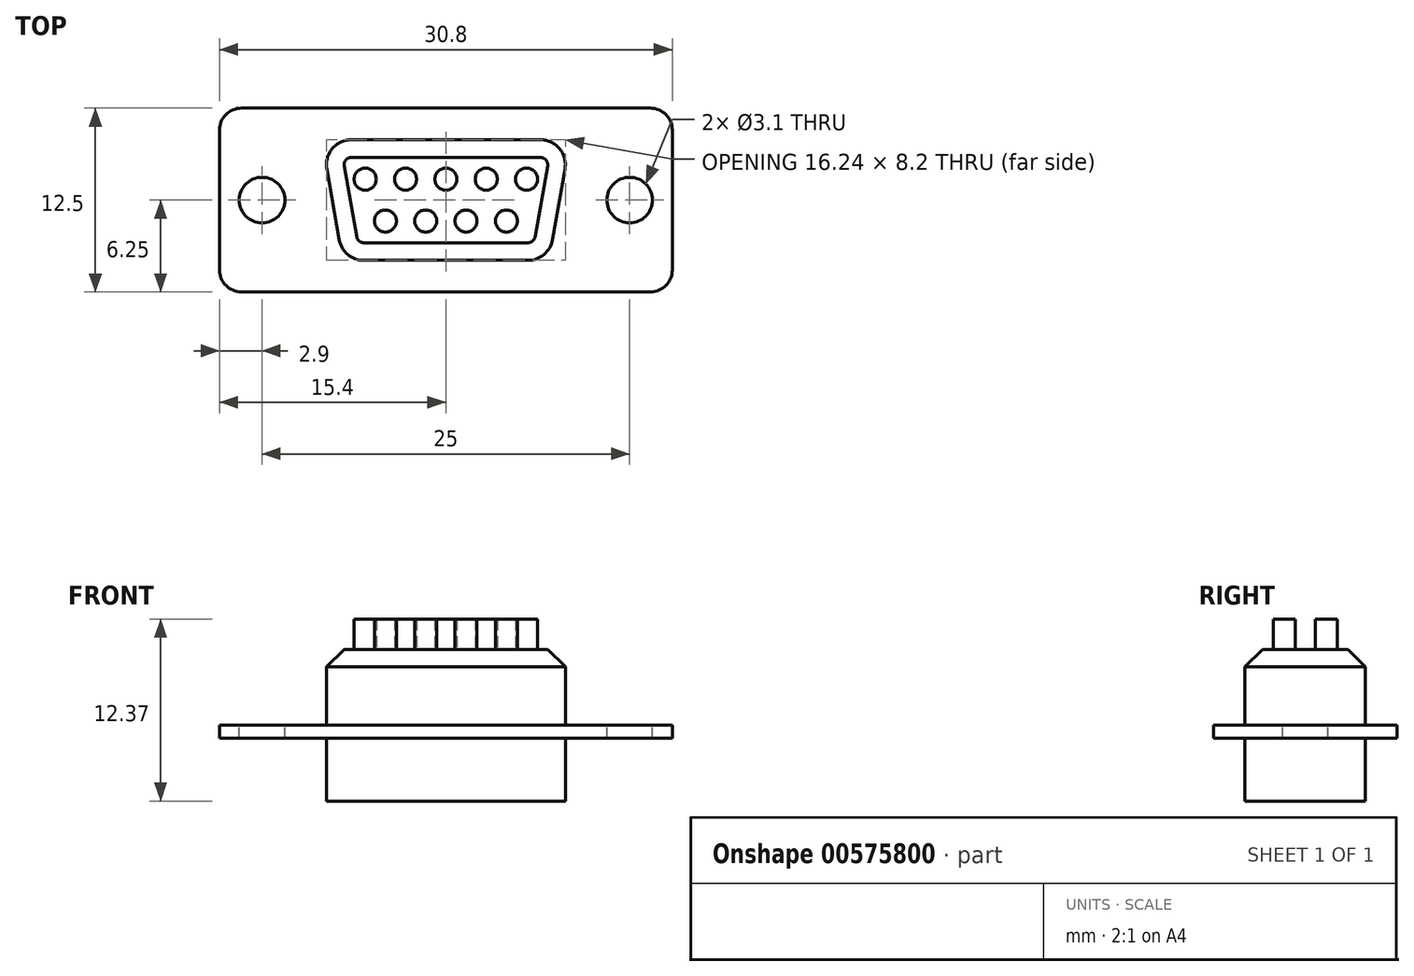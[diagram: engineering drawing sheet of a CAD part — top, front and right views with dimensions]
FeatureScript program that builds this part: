
annotation { "Feature Type Name" : "Feature", "Feature Type Description" : "" }
export const myFeature = defineFeature(function(context is Context, id is Id, definition is map)
    precondition{}
    {
        {
            var Q0;
            Q0=qCreatedBy(makeId("Top.planeOp"),FACE);
            var sketch = newSketch(context, id + "F0", { "sketchPlane" : qUnion([Q0])});
            skLineSegment(sketch, "E0.bottom", {"start": v(15.4, 6.25) * mm, "end": v(-15.4, 6.25) * mm});
            skLineSegment(sketch, "E0.top", {"start": v(15.4, -6.25) * mm, "end": v(-15.4, -6.25) * mm});
            skLineSegment(sketch, "E0.left", {"start": v(15.4, 6.25) * mm, "end": v(15.4, -6.25) * mm});
            skLineSegment(sketch, "E0.right", {"start": v(-15.4, 6.25) * mm, "end": v(-15.4, -6.25) * mm});
            skPoint(sketch, "E0.middle", {"position": v(0, 0) * mm});
            skSolve(sketch);
        }
        {
            var Q0;
            Q0=makeQuery(id+"F0.imprint","IMPRINT",FACE,{"disambiguationData":[TD([[makeQuery(id+"F0.imprint","IMPRINT",EDGE,{"derivedFrom":sQuery(id+"F0.wireOp",EDGE,"E0.bottom")}),1.0]])]});
            extrude(context, id + "F1", {"entities" : qUnion([Q0]), "depth" : 0.9 * mm, "offsetDistance" : 25.4 * mm});
        }
        {
            var Q0;
            Q0=makeQuery(id+"F1.opExtrude","SWEPT_EDGE",EDGE,{"disambiguationData":[OSD([sQuery(id+"F0.wireOp",EDGE,"E0.bottom"),sQuery(id+"F0.wireOp",EDGE,"E0.right")])]});
            var Q1;
            Q1=makeQuery(id+"F1.opExtrude","SWEPT_EDGE",EDGE,{"disambiguationData":[OSD([sQuery(id+"F0.wireOp",EDGE,"E0.bottom"),sQuery(id+"F0.wireOp",EDGE,"E0.left")])]});
            var Q2;
            Q2=makeQuery(id+"F1.opExtrude","SWEPT_EDGE",EDGE,{"disambiguationData":[OSD([sQuery(id+"F0.wireOp",EDGE,"E0.top"),sQuery(id+"F0.wireOp",EDGE,"E0.left")])]});
            var Q3;
            Q3=makeQuery(id+"F1.opExtrude","SWEPT_EDGE",EDGE,{"disambiguationData":[OSD([sQuery(id+"F0.wireOp",EDGE,"E0.top"),sQuery(id+"F0.wireOp",EDGE,"E0.right")])]});
            fillet(context, id + "F2", {"entities" : qUnion([Q0, Q1, Q2, Q3]), "radius" : 1.5 * mm, "tangentPropagation" : true, "allowEdgeOverflow" : false});
        }
        {
            var Q0;
            Q0=makeQuery(id+"F1.opExtrude","CAP_FACE",FACE,{"disambiguationData":[OSD([sQuery(id+"F0.wireOp",EDGE,"E0.bottom"),sQuery(id+"F0.wireOp",EDGE,"E0.top"),sQuery(id+"F0.wireOp",EDGE,"E0.left"),sQuery(id+"F0.wireOp",EDGE,"E0.right")])],"isStart":false});
            var sketch = newSketch(context, id + "F3", { "sketchPlane" : qUnion([Q0])});
            skLineSegment(sketch, "E1.bottom", {"start": v(8.45, 4.1) * mm, "end": v(-8.45, 4.1) * mm, "construction": true});
            skLineSegment(sketch, "E1.top", {"start": v(8.45, -4.1) * mm, "end": v(-8.45, -4.1) * mm, "construction": true});
            skLineSegment(sketch, "E1.left", {"start": v(8.45, 4.1) * mm, "end": v(8.45, -4.1) * mm, "construction": true});
            skLineSegment(sketch, "E1.right", {"start": v(-8.45, 4.1) * mm, "end": v(-8.45, -4.1) * mm, "construction": true});
            skPoint(sketch, "E1.middle", {"position": v(0, 0) * mm});
            skLineSegment(sketch, "E2", {"start": v(-8.45, 4.1) * mm, "end": v(8.45, 4.1) * mm});
            skLineSegment(sketch, "E3", {"start": v(-8.45, 4.1) * mm, "end": v(-7, -4.1) * mm});
            skLineSegment(sketch, "E4", {"start": v(8.45, 4.1) * mm, "end": v(7, -4.1) * mm});
            skLineSegment(sketch, "E5", {"start": v(-7, -4.1) * mm, "end": v(7, -4.1) * mm});
            skSolve(sketch);
        }
        {
            var Q0;
            Q0=makeQuery(id+"F3.imprint","IMPRINT",FACE,{"disambiguationData":[TD([[makeQuery(id+"F3.imprint","IMPRINT",EDGE,{"derivedFrom":sQuery(id+"F3.wireOp",EDGE,"E2")}),-1.0]])]});
            extrude(context, id + "F4", {"entities" : qUnion([Q0]), "operationType" : NewBodyOperationType.ADD, "endBound" : BoundingType.SYMMETRIC, "depth" : 10.32 * mm, "offsetDistance" : 25.4 * mm});
        }
        {
            var Q0;
            Q0=makeQuery(id+"F4.opExtrude","SWEPT_EDGE",EDGE,{"disambiguationData":[OSD([sQuery(id+"F3.wireOp",EDGE,"E2"),sQuery(id+"F3.wireOp",EDGE,"E3")])]});
            var Q1;
            Q1=makeQuery(id+"F4.opExtrude","SWEPT_EDGE",EDGE,{"disambiguationData":[OSD([sQuery(id+"F3.wireOp",EDGE,"E2"),sQuery(id+"F3.wireOp",EDGE,"E4")])]});
            var Q2;
            Q2=makeQuery(id+"F4.opExtrude","SWEPT_EDGE",EDGE,{"disambiguationData":[OSD([sQuery(id+"F3.wireOp",EDGE,"E3"),sQuery(id+"F3.wireOp",EDGE,"E5")])]});
            var Q3;
            Q3=makeQuery(id+"F4.opExtrude","SWEPT_EDGE",EDGE,{"disambiguationData":[OSD([sQuery(id+"F3.wireOp",EDGE,"E4"),sQuery(id+"F3.wireOp",EDGE,"E5")])]});
            fillet(context, id + "F5", {"entities" : qUnion([Q0, Q1, Q2, Q3]), "radius" : 1.7 * mm, "tangentPropagation" : true, "allowEdgeOverflow" : false});
        }
        {
            var Q0;
            Q0=makeQuery(id+"F4.opExtrude","CAP_EDGE",EDGE,{"disambiguationData":[OSD([sQuery(id+"F3.wireOp",EDGE,"E2")])],"isStart":false});
            chamfer(context, id + "F6", {"entities" : qUnion([Q0]), "width" : 1.2 * mm, "tangentPropagation" : true});
        }
        {
            var Q0;
            Q0=makeQuery(id+"F4.opExtrude","CAP_FACE",FACE,{"disambiguationData":[OSD([sQuery(id+"F3.wireOp",EDGE,"E2"),sQuery(id+"F3.wireOp",EDGE,"E3"),sQuery(id+"F3.wireOp",EDGE,"E4"),sQuery(id+"F3.wireOp",EDGE,"E5")])],"isStart":false});
            var sketch = newSketch(context, id + "F7", { "sketchPlane" : qUnion([Q0])});
            skCircle(sketch, "E6", {"center": v(-5.49, 1.42) * mm, "radius": 0.75 * mm});
            skCircle(sketch, "E7", {"center": v(-2.74, 1.42) * mm, "radius": 0.75 * mm});
            skCircle(sketch, "E8", {"center": v(0, 1.42) * mm, "radius": 0.75 * mm});
            skCircle(sketch, "E9", {"center": v(2.74, 1.42) * mm, "radius": 0.75 * mm});
            skCircle(sketch, "E10", {"center": v(5.49, 1.42) * mm, "radius": 0.75 * mm});
            skCircle(sketch, "E11", {"center": v(-4.11, -1.42) * mm, "radius": 0.75 * mm});
            skCircle(sketch, "E12", {"center": v(-1.37, -1.42) * mm, "radius": 0.75 * mm});
            skCircle(sketch, "E13", {"center": v(1.37, -1.42) * mm, "radius": 0.75 * mm});
            skCircle(sketch, "E14", {"center": v(4.11, -1.42) * mm, "radius": 0.75 * mm});
            skLineSegment(sketch, "E15", {"start": v(-12.24, 1.42) * mm, "end": v(12.53, 1.42) * mm, "construction": true});
            skLineSegment(sketch, "E16", {"start": v(-4.11, -1.42) * mm, "end": v(4.11, -1.42) * mm, "construction": true});
            skLineSegment(sketch, "E17", {"start": v(-9.5, 0) * mm, "end": v(9.3, 0) * mm, "construction": true});
            skLineSegment(sketch, "E18", {"start": v(0, 2.68) * mm, "end": v(0, -2.04) * mm, "construction": true});
            skSolve(sketch);
        }
        {
            var Q0;
            Q0=makeQuery(id+"F7.imprint","IMPRINT",FACE,{"disambiguationData":[TD([[makeQuery(id+"F7.imprint","IMPRINT",EDGE,{"derivedFrom":sQuery(id+"F7.wireOp",EDGE,"E6")}),1.0]])]});
            var Q1;
            Q1=makeQuery(id+"F7.imprint","IMPRINT",FACE,{"disambiguationData":[TD([[makeQuery(id+"F7.imprint","IMPRINT",EDGE,{"derivedFrom":sQuery(id+"F7.wireOp",EDGE,"E7")}),1.0]])]});
            var Q2;
            Q2=makeQuery(id+"F7.imprint","IMPRINT",FACE,{"disambiguationData":[TD([[makeQuery(id+"F7.imprint","IMPRINT",EDGE,{"derivedFrom":sQuery(id+"F7.wireOp",EDGE,"E8")}),1.0]])]});
            var Q3;
            Q3=makeQuery(id+"F7.imprint","IMPRINT",FACE,{"disambiguationData":[TD([[makeQuery(id+"F7.imprint","IMPRINT",EDGE,{"derivedFrom":sQuery(id+"F7.wireOp",EDGE,"E9")}),1.0]])]});
            var Q4;
            Q4=makeQuery(id+"F7.imprint","IMPRINT",FACE,{"disambiguationData":[TD([[makeQuery(id+"F7.imprint","IMPRINT",EDGE,{"derivedFrom":sQuery(id+"F7.wireOp",EDGE,"E10")}),1.0]])]});
            var Q5;
            Q5=makeQuery(id+"F7.imprint","IMPRINT",FACE,{"disambiguationData":[TD([[makeQuery(id+"F7.imprint","IMPRINT",EDGE,{"derivedFrom":sQuery(id+"F7.wireOp",EDGE,"E14")}),1.0]])]});
            var Q6;
            Q6=makeQuery(id+"F7.imprint","IMPRINT",FACE,{"disambiguationData":[TD([[makeQuery(id+"F7.imprint","IMPRINT",EDGE,{"derivedFrom":sQuery(id+"F7.wireOp",EDGE,"E13")}),1.0]])]});
            var Q7;
            Q7=makeQuery(id+"F7.imprint","IMPRINT",FACE,{"disambiguationData":[TD([[makeQuery(id+"F7.imprint","IMPRINT",EDGE,{"derivedFrom":sQuery(id+"F7.wireOp",EDGE,"E12")}),1.0]])]});
            var Q8;
            Q8=makeQuery(id+"F7.imprint","IMPRINT",FACE,{"disambiguationData":[TD([[makeQuery(id+"F7.imprint","IMPRINT",EDGE,{"derivedFrom":sQuery(id+"F7.wireOp",EDGE,"E11")}),1.0]])]});
            extrude(context, id + "F8", {"entities" : qUnion([Q0, Q1, Q2, Q3, Q4, Q5, Q6, Q7, Q8]), "operationType" : NewBodyOperationType.ADD, "depth" : 2.05 * mm, "offsetDistance" : 25.4 * mm});
        }
        {
            var Q0;
            Q0=makeQuery(id+"F1.opExtrude","CAP_FACE",FACE,{"disambiguationData":[OSD([sQuery(id+"F0.wireOp",EDGE,"E0.bottom"),sQuery(id+"F0.wireOp",EDGE,"E0.top"),sQuery(id+"F0.wireOp",EDGE,"E0.left"),sQuery(id+"F0.wireOp",EDGE,"E0.right")])],"isStart":false});
            var sketch = newSketch(context, id + "F9", { "sketchPlane" : qUnion([Q0])});
            skCircle(sketch, "E19", {"center": v(-12.5, 0) * mm, "radius": 1.55 * mm});
            skCircle(sketch, "E20", {"center": v(12.5, 0) * mm, "radius": 1.55 * mm});
            skSolve(sketch);
        }
        {
            var Q0;
            Q0=makeQuery(id+"F9.imprint","IMPRINT",FACE,{"disambiguationData":[TD([[makeQuery(id+"F9.imprint","IMPRINT",EDGE,{"derivedFrom":sQuery(id+"F9.wireOp",EDGE,"E19")}),1.0]])]});
            var Q1;
            Q1=makeQuery(id+"F9.imprint","IMPRINT",FACE,{"disambiguationData":[TD([[makeQuery(id+"F9.imprint","IMPRINT",EDGE,{"derivedFrom":sQuery(id+"F9.wireOp",EDGE,"E20")}),1.0]])]});
            extrude(context, id + "F10", {"entities" : qUnion([Q0, Q1]), "operationType" : NewBodyOperationType.REMOVE, "oppositeDirection" : true, "depth" : 0.9 * mm, "offsetDistance" : 25.4 * mm});
        }
    });
